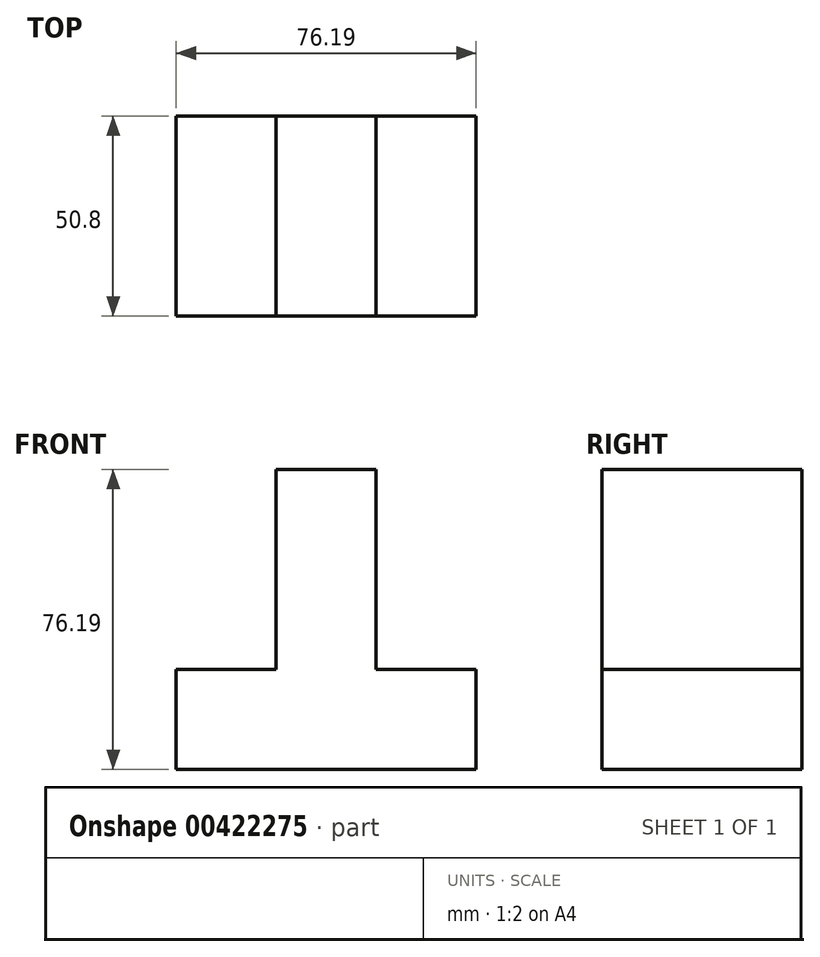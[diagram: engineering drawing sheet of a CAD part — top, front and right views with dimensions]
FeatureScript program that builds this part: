
annotation { "Feature Type Name" : "Feature", "Feature Type Description" : "" }
export const myFeature = defineFeature(function(context is Context, id is Id, definition is map)
    precondition{}
    {
        {
            var Q0;
            Q0=qCreatedBy(makeId("Front.planeOp"),FACE);
            var sketch = newSketch(context, id + "F0", { "sketchPlane" : qUnion([Q0])});
            skLineSegment(sketch, "E0", {"start": v(48.31, -32.46) * mm, "end": v(-27.88, -32.46) * mm});
            skLineSegment(sketch, "E1", {"start": v(-27.88, -32.46) * mm, "end": v(-27.88, -7.07) * mm});
            skLineSegment(sketch, "E2", {"start": v(-27.88, -7.07) * mm, "end": v(-2.48, -7.07) * mm});
            skLineSegment(sketch, "E3", {"start": v(-2.48, -7.07) * mm, "end": v(-2.48, 43.73) * mm});
            skLineSegment(sketch, "E4", {"start": v(-2.48, 43.73) * mm, "end": v(22.91, 43.73) * mm});
            skLineSegment(sketch, "E5", {"start": v(22.91, 43.73) * mm, "end": v(22.91, -7.07) * mm});
            skLineSegment(sketch, "E6", {"start": v(22.91, -7.07) * mm, "end": v(48.31, -7.07) * mm});
            skLineSegment(sketch, "E7", {"start": v(48.31, -7.07) * mm, "end": v(48.31, -32.46) * mm});
            skSolve(sketch);
        }
        {
            var Q0;
            Q0=makeQuery(id+"F0.imprint","IMPRINT",FACE,{"disambiguationData":[TD([[makeQuery(id+"F0.imprint","IMPRINT",EDGE,{"derivedFrom":sQuery(id+"F0.wireOp",EDGE,"E0")}),-1.0]])]});
            extrude(context, id + "F1", {"entities" : qUnion([Q0]), "depth" : 50.8 * mm});
        }
    });
